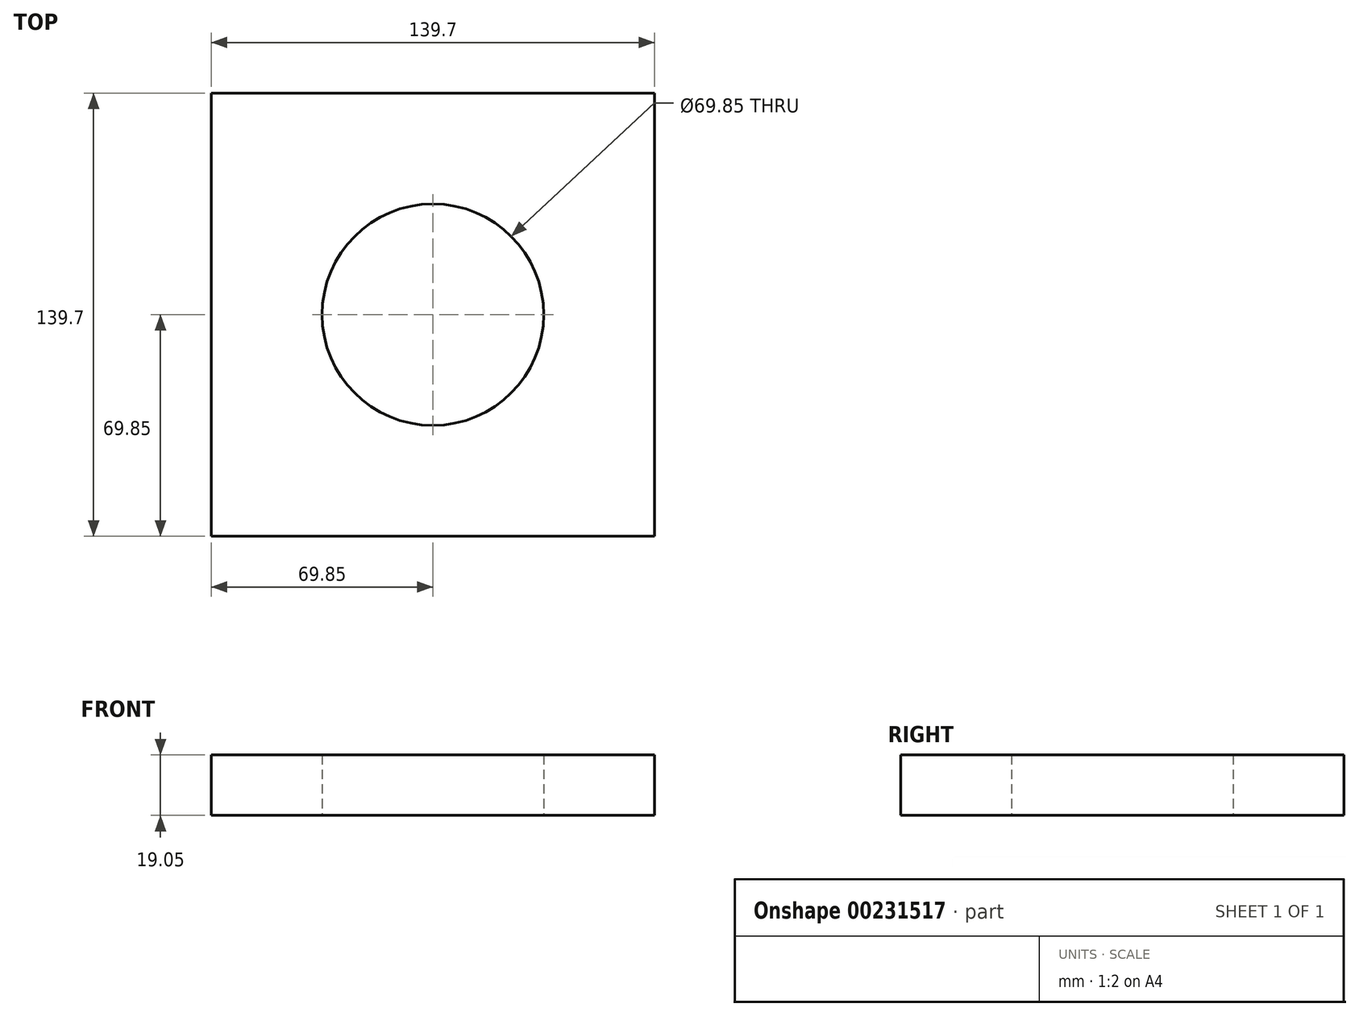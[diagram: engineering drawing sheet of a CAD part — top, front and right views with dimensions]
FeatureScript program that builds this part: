
annotation { "Feature Type Name" : "Feature", "Feature Type Description" : "" }
export const myFeature = defineFeature(function(context is Context, id is Id, definition is map)
    precondition{}
    {
        {
            var Q0;
            Q0=qCreatedBy(makeId("Top.planeOp"),FACE);
            var sketch = newSketch(context, id + "F0", { "sketchPlane" : qUnion([Q0])});
            skLineSegment(sketch, "E0.bottom", {"start": v(69.85, -69.85) * mm, "end": v(-69.85, -69.85) * mm});
            skLineSegment(sketch, "E0.top", {"start": v(69.85, 69.85) * mm, "end": v(-69.85, 69.85) * mm});
            skLineSegment(sketch, "E0.left", {"start": v(69.85, -69.85) * mm, "end": v(69.85, 69.85) * mm});
            skLineSegment(sketch, "E0.right", {"start": v(-69.85, -69.85) * mm, "end": v(-69.85, 69.85) * mm});
            skPoint(sketch, "E0.middle", {"position": v(0, 0) * mm});
            skCircle(sketch, "E1", {"center": v(0, 0) * mm, "radius": 34.93 * mm});
            skSolve(sketch);
        }
        {
            var Q0;
            Q0=makeQuery(id+"F0.imprint","IMPRINT",FACE,{"disambiguationData":[TD([[makeQuery(id+"F0.imprint","IMPRINT",EDGE,{"derivedFrom":sQuery(id+"F0.wireOp",EDGE,"E0.bottom")}),-1.0]])]});
            extrude(context, id + "F1", {"entities" : qUnion([Q0]), "depth" : 19.05 * mm});
        }
    });
